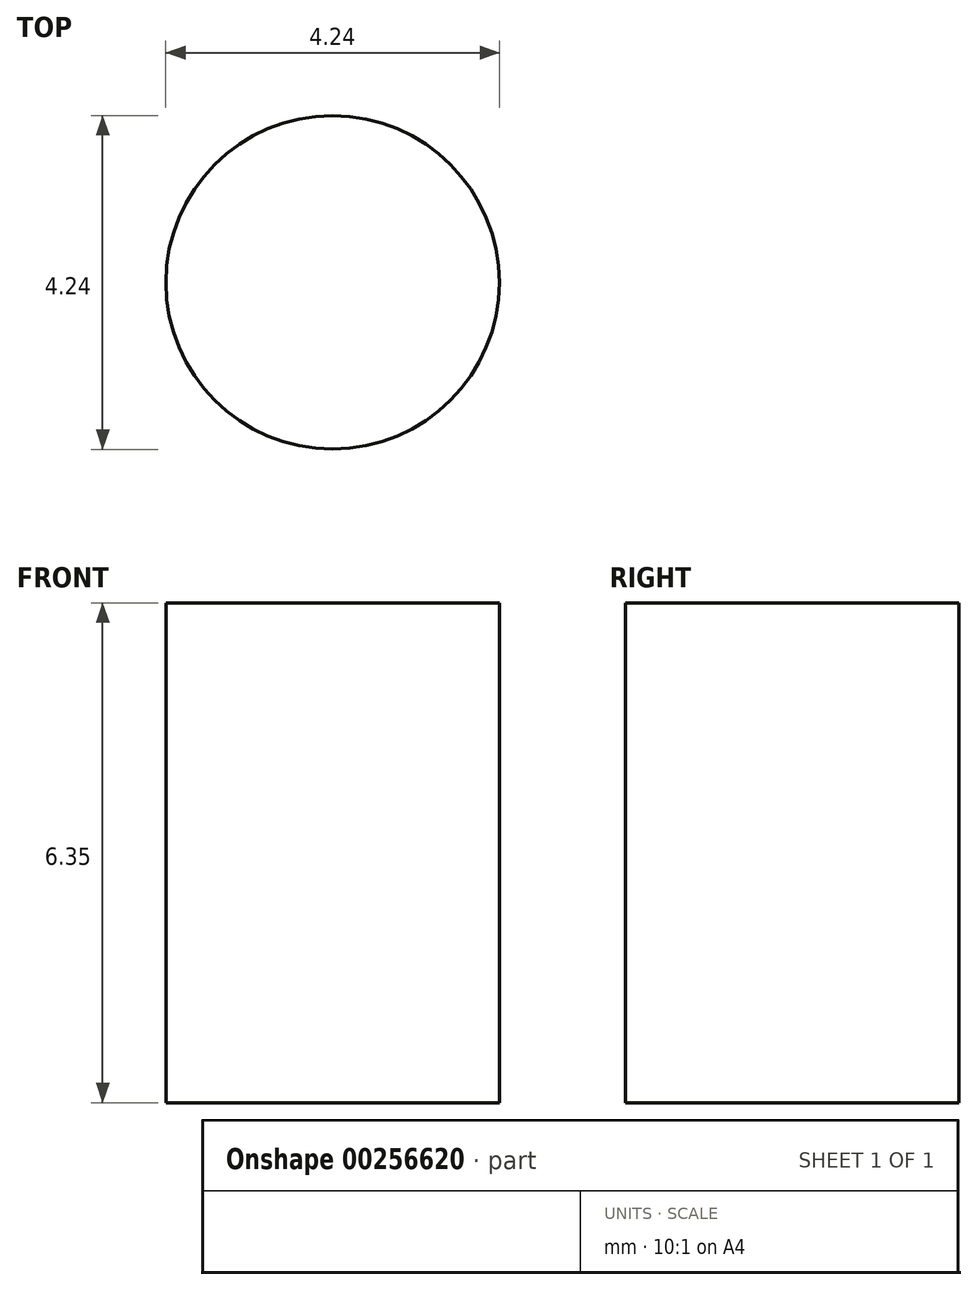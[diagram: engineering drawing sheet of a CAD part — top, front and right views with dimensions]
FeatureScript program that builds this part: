
annotation { "Feature Type Name" : "Feature", "Feature Type Description" : "" }
export const myFeature = defineFeature(function(context is Context, id is Id, definition is map)
    precondition{}
    {
        {
            var Q0;
            Q0=qCreatedBy(makeId("Top.planeOp"),FACE);
            var sketch = newSketch(context, id + "F0", { "sketchPlane" : qUnion([Q0])});
            skCircle(sketch, "E0", {"center": v(0, 0) * mm, "radius": 2.12 * mm});
            skSolve(sketch);
        }
        {
            var Q0;
            Q0=makeQuery(id+"F0.imprint","IMPRINT",FACE,{"disambiguationData":[TD([[makeQuery(id+"F0.imprint","IMPRINT",EDGE,{"derivedFrom":sQuery(id+"F0.wireOp",EDGE,"E0")}),1.0]])]});
            extrude(context, id + "F1", {"entities" : qUnion([Q0]), "depth" : 6.35 * mm});
        }
    });
